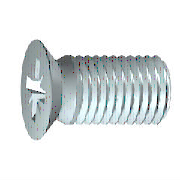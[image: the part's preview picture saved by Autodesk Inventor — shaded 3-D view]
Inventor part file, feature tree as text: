
AUTODESK INVENTOR PART (.ipt)
format: ipt  version: 2025.2 (Build 292293000, 293)  size: 204,800 bytes
history: native  units: mm (DEFAULTED — no unit token found)
features: other x7, pattern_circular x1, plane x1
ambient origin geometry x7: Origin, YZ Plane, XY Plane, X Axis, Y Axis, Z Axis, Center Point
bodies: Solid1 (feature_tree)
feature tree (9):
  other  "WorkPoint1"
  other  "WorkPoint2"
  other  "Drehung1"
  other  "Work Axis1"
  pattern_circular  "Polare Anordnung1"  [2 undecoded]
  other  "MSC_A1"
  other  "MSC_PF1"
  other  "MSC_PT1"
  plane  "WorkPlane1"
note: 2 required parameter values undecoded (feature->parameter linkage not recoverable at this tier; creation-order binding heuristic only, values carry confidence <= 0.55)
